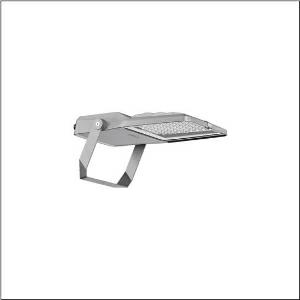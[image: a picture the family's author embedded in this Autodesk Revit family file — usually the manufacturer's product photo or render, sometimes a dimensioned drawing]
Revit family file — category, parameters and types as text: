
# Revit family: floodlight_fl_21_iq_mini___pl43_5xa7772d5a1a_690f
name_source: partatom
category: Lighting Fixtures
units: mm (PartAtom-declared; Revit-internal decimal feet)

## family parameters
Cut with Voids When Loaded = No
Host = Face
Light Source = No
Part Type = Normal
Room Calculation Point = No
Round Connector Dimension = Use Diameter
Shared = No

## types (1)
- --- (1 x LED, 17070 lm, 143 W, 4000K)
    Apparent Load = 143 VA
    CIE Flux Codes = 27 78 99 100 100
    Color Rendering = 80
    Color Temperature = 4000K
    Default Elevation = 1800 mm
    Description = Floodlight FL 21 iQ mini, floodlight, primary light control with lens, of PMMA, primary optical cover: protective disc, of toughened safety glass, transparent, light distribution: PL43, light emission: direct distribution, installation type: surface-mounted, LED, High Power LED, rated luminous flux: 17.070lm, luminous efficacy: 119lm/W, light colour: 840, colour temperature: 4000K, control gear: iQ Street-Remote/DALI, control: Street-Remote, Auto-Match, Temp-Guard, Night-Set, Smart-Wire, Desk-Remote (wireless, voltage-free reading and setting of iQ features in the workshop via application-optimized NFC function/RFID function), optimised constant luminous flux control (CLO 2.0), with terminal, 6-pole, mains connection: 220..240V, AC, 50/60Hz, start of lifetime: 143W, end of service life: 152W, reduction: 61W, luminaire housing, of diecast aluminium, powder-coated, Siteco® metallic grey (DB 702S), corrosivity category C5 mid according to DIN EN ISO 12944, suitable for swimming pools, chlorine-resistant, sealing non-destructively replaceable, mounting bracket, of steel, galvanised, powder-coated, Siteco® metallic grey (DB 702S), protection rating (complete): IP66, insulation class (complete): insulation class II (safety insulation), certification: CE, ENEC, VDE, protection symbol: D, impact resistance: IK08, permissible operating ambient temperature: -40..+40°C, permissible operating ambient temperature for outdoor applications: -40..+50°C, standard: DIN EN 12944, LABS conformity tested according to VDMA 24364:2018-05, packaging unit: 1 piece

Light Distribution: PL43
    Height = 70 mm
    Lamp = 1 x LED
    Lamp Light Flux = 17070 lm
    Lamp Power = 143 W
    Lamp count = 1
    Length = 485 mm
    Luminous efficacy = 119 lm/W
    Manufacturer = Siteco
    ModVariant = No
    Model = 5XA7772D5A1A
    Number of Poles = 1
    OnlyDefault = Yes
    Power Factor = 1
    Product Name = Floodlight FL 21 iQ mini | PL43
    Product group = floodlight | pylon annexe
    ProductGroupID = 6200
    Protection Class = Protection class II
    Protection Degree = IP 66
    RLX_Detail_Level = 1
    RLX_Emergency_Light_Flux = 0 lm
    RLX_Emergency_Type = 0
    RLX_Emergency_Type_DB = No
    RlxData = <blob elided: 96501 chars, md5=eb9fe84a>
    Socket = socket
    Standby Power = 0 W
    System Light Flux = 17070 lm
    System Power = 143 W
    Type Comments = factory setting: luminous flux: 100 % | dim-lin: 254 | 730 mA
    Type Image = l_1006845.jpg
    URL = http://relux.com
    VarID = @adj_161436
    Voltage = 0 V
    Weight = 0.00 kg
    Width = 337 mm

## geometry (parser evidence)
native form markers: Blend x4, Sweep x12
no freeform markers — native parametric forms only
